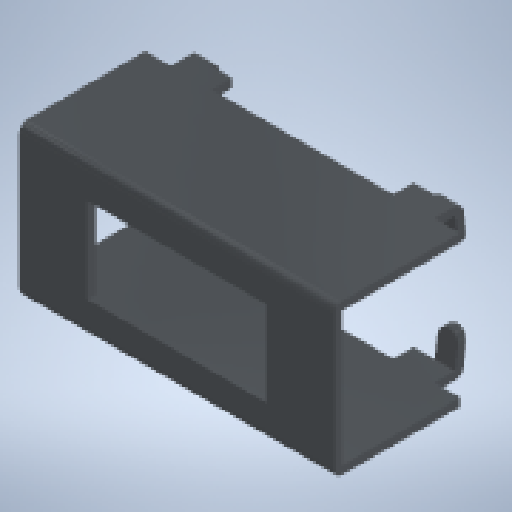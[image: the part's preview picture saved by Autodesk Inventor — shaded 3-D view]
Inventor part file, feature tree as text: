
AUTODESK INVENTOR PART (.ipt)
format: ipt  version: 2024.3 (Build 283343000, 343)  size: 198,656 bytes
history: native  units: in
note: dims shown in document units (in); Inventor stores cm internally (conversion verified against a paired STEP export)
features: projected_geometry x4, extrude x1, sketch x1, imported_body x1
ambient origin geometry x8: Origin, YZ Plane, XZ Plane, XY Plane, X Axis, Y Axis, Z Axis, Center Point
bodies: Solid1 (feature_tree)
feature tree (7):
  extrude  "Extrusion1"  [1 undecoded]
  sketch  "Sketch1"  dims[d0=0.0in d1=0.0in]
  projected_geometry  "Projected Loop1"
  projected_geometry  "Projected Loop2"
  projected_geometry  "Projected Loop3"
  projected_geometry  "Projected Loop4"
  imported_body  "Base1"
note: 1 required parameter value undecoded (feature->parameter linkage not recoverable at this tier; creation-order binding heuristic only, values carry confidence <= 0.55)
